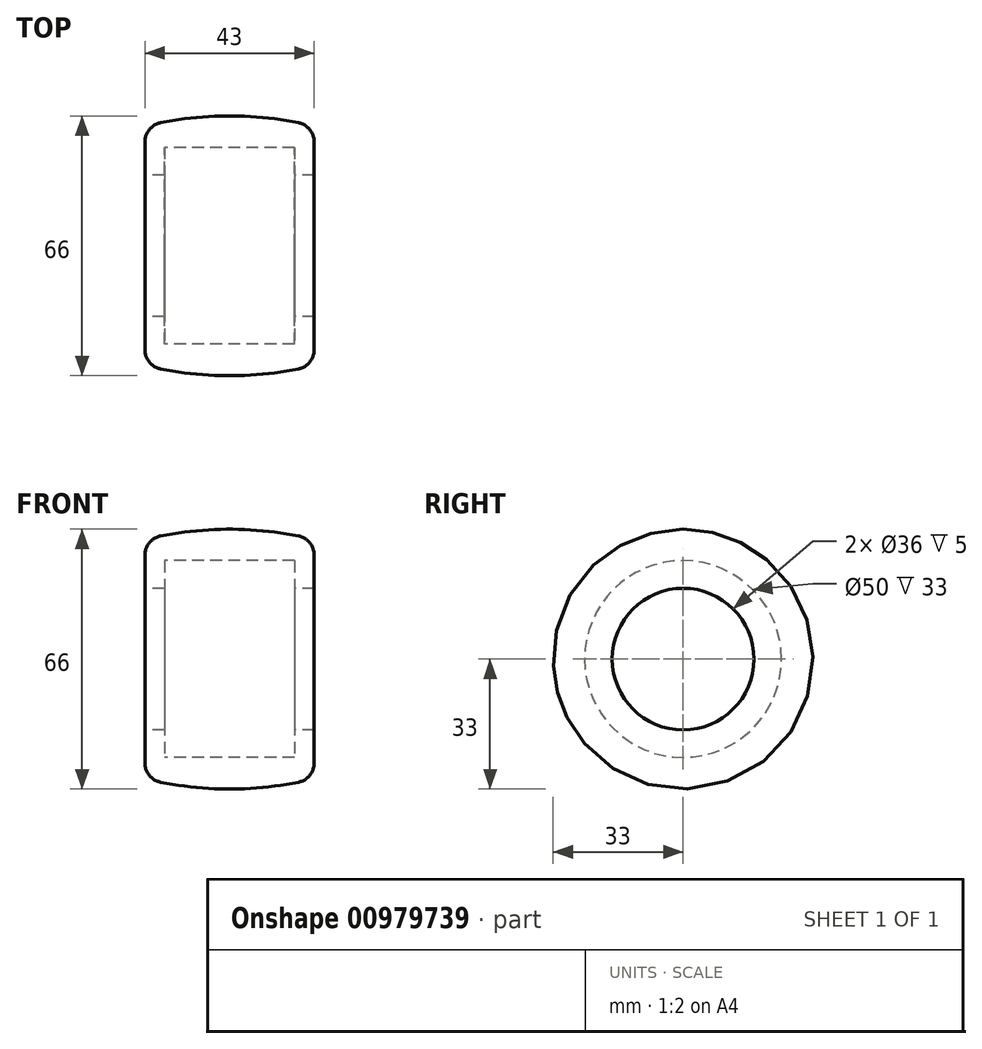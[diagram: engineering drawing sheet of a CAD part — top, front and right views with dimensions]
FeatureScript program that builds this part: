
annotation { "Feature Type Name" : "Feature", "Feature Type Description" : "" }
export const myFeature = defineFeature(function(context is Context, id is Id, definition is map)
    precondition{}
    {
        {
            var Q0;
            Q0=qCreatedBy(makeId("Front.planeOp"),FACE);
            var sketch = newSketch(context, id + "F0", { "sketchPlane" : qUnion([Q0])});
            skLineSegment(sketch, "E0.left", {"start": v(-21.5, 18) * mm, "end": v(-21.5, 26.38) * mm});
            skPoint(sketch, "E1.center.orphan", {"position": v(0, -57) * mm});
            skPoint(sketch, "E2.start.orphan", {"position": v(-44.08, 0) * mm});
            skArc(sketch, "E3", {"start": v(17.47, 31.29) * mm, "mid": v(0, 33) * mm, "end": v(-17.47, 31.29) * mm});
            skLineSegment(sketch, "E4", {"start": v(21.5, 26.38) * mm, "end": v(21.5, 18) * mm});
            skArc(sketch, "E5", {"start": v(-17.47, 31.29) * mm, "mid": v(-20.36, 29.56) * mm, "end": v(-21.5, 26.38) * mm});
            skArc(sketch, "E6", {"start": v(21.5, 26.38) * mm, "mid": v(20.36, 29.56) * mm, "end": v(17.47, 31.29) * mm});
            skLineSegment(sketch, "E7", {"start": v(-44.08, 0) * mm, "end": v(-21.5, 0) * mm, "construction": true});
            skLineSegment(sketch, "E8.bottom", {"start": v(16.5, 25) * mm, "end": v(-16.5, 25) * mm});
            skLineSegment(sketch, "E8.left", {"start": v(16.5, 25) * mm, "end": v(16.5, 18) * mm});
            skLineSegment(sketch, "E8.right", {"start": v(-16.5, 25) * mm, "end": v(-16.5, 18) * mm});
            skPoint(sketch, "E8.middle", {"position": v(0, 0) * mm});
            skLineSegment(sketch, "E9", {"start": v(-21.5, 18) * mm, "end": v(-16.5, 18) * mm});
            skPoint(sketch, "E8.top.end.orphan", {"position": v(-16.5, -25) * mm});
            skPoint(sketch, "E10.orphan", {"position": v(16.5, -25) * mm});
            skLineSegment(sketch, "E11.trimOffspring", {"start": v(21.5, 0) * mm, "end": v(42.56, 0) * mm, "construction": true});
            skLineSegment(sketch, "E12.trimOffspring", {"start": v(16.5, 18) * mm, "end": v(21.5, 18) * mm});
            skSolve(sketch);
        }
        {
            var Q0;
            Q0=qSketchRegion(id+"F0",true);
            var Q1;
            Q1=sQuery(id+"F0.wireOp",EDGE,"E7");
            revolve(context, id + "F1", {"surfaceOperationType" : NewSurfaceOperationType.NEW, "entities" : qUnion([Q0]), "axis" : qUnion([Q1]), "revolveType" : RevolveType.FULL});
        }
    });
